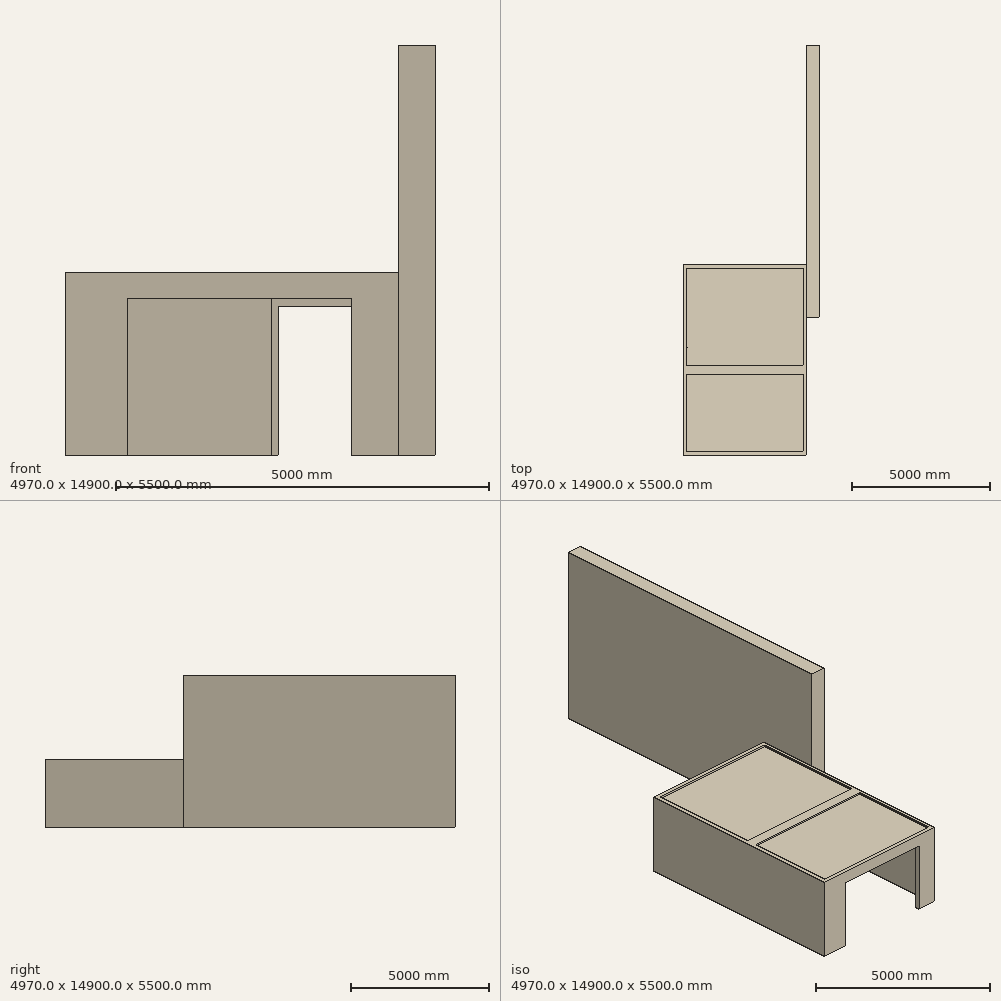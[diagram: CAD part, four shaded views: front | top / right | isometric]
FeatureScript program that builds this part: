
annotation { "Feature Type Name" : "Feature", "Feature Type Description" : "" }
export const myFeature = defineFeature(function(context is Context, id is Id, definition is map)
    precondition{}
    {
        {
            var Q0;
            Q0=qCreatedBy(makeId("Top.planeOp"),FACE);
            var sketch = newSketch(context, id + "F0", { "sketchPlane" : qUnion([Q0])});
            skLineSegment(sketch, "E0.rect.bottom", {"start": v(2235, -3475) * mm, "end": v(-2235, -3475) * mm});
            skLineSegment(sketch, "E0.rect.top", {"start": v(2235, 3475) * mm, "end": v(-2235, 3475) * mm});
            skLineSegment(sketch, "E0.rect.left", {"start": v(2235, -3475) * mm, "end": v(2235, 3475) * mm});
            skLineSegment(sketch, "E0.rect.right", {"start": v(-2235, -3475) * mm, "end": v(-2235, 3475) * mm});
            skPoint(sketch, "E0.rect.middle", {"position": v(0, 0) * mm});
            skLineSegment(sketch, "E1", {"start": v(2135, 3335) * mm, "end": v(-2095, 3335) * mm});
            skLineSegment(sketch, "E2", {"start": v(-2095, 3335) * mm, "end": v(-2095, -215) * mm});
            skLineSegment(sketch, "E3", {"start": v(-2095, -535) * mm, "end": v(-2095, -3335) * mm});
            skLineSegment(sketch, "E4", {"start": v(-2095, -3335) * mm, "end": v(2135, -3335) * mm});
            skLineSegment(sketch, "E5", {"start": v(-2095, -215) * mm, "end": v(-2095, -535) * mm});
            skLineSegment(sketch, "E6", {"start": v(-2095, -215) * mm, "end": v(1703, -215) * mm});
            skLineSegment(sketch, "E7", {"start": v(1703, -535) * mm, "end": v(-2095, -535) * mm});
            skLineSegment(sketch, "E8", {"start": v(2135, 3335) * mm, "end": v(2135, -215) * mm});
            skLineSegment(sketch, "E9", {"start": v(2135, -215) * mm, "end": v(1703, -215) * mm});
            skLineSegment(sketch, "E10", {"start": v(2135, -3335) * mm, "end": v(2135, -535) * mm});
            skLineSegment(sketch, "E11", {"start": v(2135, -535) * mm, "end": v(1703, -535) * mm});
            skLineSegment(sketch, "E12", {"start": v(1703, -215) * mm, "end": v(1703, -535) * mm});
            skSolve(sketch);
        }
        {
            var Q0;
            Q0=makeQuery(id+"F0.imprint","IMPRINT",FACE,{"disambiguationData":[TD([[makeQuery(id+"F0.imprint","IMPRINT",EDGE,{"derivedFrom":sQuery(id+"F0.wireOp",EDGE,"E0.rect.bottom")}),-1.0]])]});
            extrude(context, id + "F1", {"entities" : qUnion([Q0]), "oppositeDirection" : true, "depth" : 2280 * mm});
        }
        {
            var Q0;
            Q0=makeQuery(id+"F0.imprint","IMPRINT",FACE,{"disambiguationData":[TD([[makeQuery(id+"F0.imprint","IMPRINT",EDGE,{"derivedFrom":sQuery(id+"F0.wireOp",EDGE,"E5")}),1.0]])]});
            extrude(context, id + "F2", {"entities" : qUnion([Q0]), "operationType" : NewBodyOperationType.ADD, "oppositeDirection" : true, "depth" : 172 * mm});
        }
        {
            var Q0;
            Q0=makeQuery(id+"F2.boolean.opBoolean","MERGE",FACE,{"derivedFrom":[makeQuery(id+"F1.opExtrude","SWEPT_FACE",FACE,{"disambiguationData":[OSD([sQuery(id+"F0.wireOp",EDGE,"E11")])]}),makeQuery(id+"F2.opExtrude","SWEPT_FACE",FACE,{"disambiguationData":[OSD([sQuery(id+"F0.wireOp",EDGE,"E7")])]})]});
            var sketch = newSketch(context, id + "F3", { "sketchPlane" : qUnion([Q0])});
            skCircle(sketch, "E13", {"center": v(1935, -310) * mm, "radius": 75 * mm});
            skSolve(sketch);
        }
        {
            var Q0;
            Q0=makeQuery(id+"F3.imprint","IMPRINT",FACE,{"disambiguationData":[TD([[makeQuery(id+"F3.imprint","IMPRINT",EDGE,{"derivedFrom":sQuery(id+"F3.wireOp",EDGE,"E13")}),1.0]])]});
            extrude(context, id + "F4", {"entities" : qUnion([Q0]), "operationType" : NewBodyOperationType.REMOVE, "endBound" : BoundingType.UP_TO_NEXT, "oppositeDirection" : true, "depth" : 25 * mm});
        }
        {
            var Q0;
            Q0=makeQuery(id+"F1.opExtrude","SWEPT_FACE",FACE,{"disambiguationData":[OSD([sQuery(id+"F0.wireOp",EDGE,"E1")])]});
            var sketch = newSketch(context, id + "F5", { "sketchPlane" : qUnion([Q0])});
            skCircle(sketch, "E14", {"center": v(-1795, -135) * mm, "radius": 60 * mm});
            skCircle(sketch, "E15", {"center": v(-1595, -135) * mm, "radius": 60 * mm});
            skSolve(sketch);
        }
        {
            var Q0;
            Q0=makeQuery(id+"F5.imprint","IMPRINT",FACE,{"disambiguationData":[TD([[makeQuery(id+"F5.imprint","IMPRINT",EDGE,{"derivedFrom":sQuery(id+"F5.wireOp",EDGE,"E14")}),1.0]])]});
            var Q1;
            Q1=makeQuery(id+"F5.imprint","IMPRINT",FACE,{"disambiguationData":[TD([[makeQuery(id+"F5.imprint","IMPRINT",EDGE,{"derivedFrom":sQuery(id+"F5.wireOp",EDGE,"E15")}),1.0]])]});
            extrude(context, id + "F6", {"entities" : qUnion([Q0, Q1]), "operationType" : NewBodyOperationType.REMOVE, "endBound" : BoundingType.UP_TO_NEXT, "oppositeDirection" : true, "depth" : 25 * mm});
        }
        {
            var Q0;
            Q0=makeQuery(id+"F1.opExtrude","SWEPT_FACE",FACE,{"disambiguationData":[OSD([sQuery(id+"F0.wireOp",EDGE,"E0.rect.bottom")])]});
            var sketch = newSketch(context, id + "F7", { "sketchPlane" : qUnion([Q0])});
            skLineSegment(sketch, "E16", {"start": v(45.5, -2280) * mm, "end": v(-1398.66, -2280) * mm});
            skLineSegment(sketch, "E17", {"start": v(-1398.66, -2280) * mm, "end": v(-1398.66, -180) * mm});
            skLineSegment(sketch, "E18", {"start": v(-1398.66, -180) * mm, "end": v(0, -180) * mm});
            skLineSegment(sketch, "E19", {"start": v(0, -180) * mm, "end": v(1601.34, -180) * mm});
            skLineSegment(sketch, "E20", {"start": v(1601.34, -180) * mm, "end": v(1601.34, -2280) * mm});
            skLineSegment(sketch, "E21", {"start": v(1601.34, -2280) * mm, "end": v(45.5, -2280) * mm});
            skLineSegment(sketch, "E22", {"start": v(-2235, 0) * mm, "end": v(-2235, 124) * mm});
            skLineSegment(sketch, "E23", {"start": v(-2235, 124) * mm, "end": v(2235, 124) * mm});
            skLineSegment(sketch, "E24", {"start": v(2235, 124) * mm, "end": v(2235, 0) * mm});
            skLineSegment(sketch, "E25", {"start": v(-2235, 124) * mm, "end": v(-2235, 174) * mm});
            skLineSegment(sketch, "E26", {"start": v(-2235, 174) * mm, "end": v(2235, 174) * mm});
            skLineSegment(sketch, "E27", {"start": v(2235, 174) * mm, "end": v(2235, 124) * mm});
            skLineSegment(sketch, "E28", {"start": v(-2235, 0) * mm, "end": v(2235, 0) * mm});
            skSolve(sketch);
        }
        {
            var Q0;
            Q0=makeQuery(id+"F7.imprint","IMPRINT",FACE,{"disambiguationData":[TD([[makeQuery(id+"F7.imprint","IMPRINT",EDGE,{"derivedFrom":sQuery(id+"F7.wireOp",EDGE,"E16")}),-1.0]])]});
            extrude(context, id + "F8", {"entities" : qUnion([Q0]), "operationType" : NewBodyOperationType.REMOVE, "endBound" : BoundingType.UP_TO_NEXT, "oppositeDirection" : true, "depth" : 25 * mm});
        }
        {
            var Q0;
            Q0=makeQuery(id+"F1.opExtrude","SWEPT_FACE",FACE,{"disambiguationData":[OSD([sQuery(id+"F0.wireOp",EDGE,"E0.rect.top")])]});
            var sketch = newSketch(context, id + "F9", { "sketchPlane" : qUnion([Q0])});
            skLineSegment(sketch, "E29", {"start": v(-1625, -2280) * mm, "end": v(-1625, -280) * mm});
            skLineSegment(sketch, "E30", {"start": v(-1625, -280) * mm, "end": v(-625, -280) * mm});
            skLineSegment(sketch, "E31", {"start": v(-625, -280) * mm, "end": v(-625, -2280) * mm});
            skSolve(sketch);
        }
        {
            var Q0;
            {var subQ2=sQuery(id+"F9.wireOp",EDGE,"E29");Q0=makeQuery(id+"F9.imprint","IMPRINT",FACE,{"disambiguationData":[TD([[makeQuery(id+"F9.imprint","IMPRINT",EDGE,{"derivedFrom":subQ2}),-1.0]])]});}
            extrude(context, id + "F10", {"entities" : qUnion([Q0]), "operationType" : NewBodyOperationType.REMOVE, "endBound" : BoundingType.UP_TO_NEXT, "oppositeDirection" : true, "depth" : 25 * mm});
        }
        {
            var Q0;
            Q0=makeQuery(id+"F0.imprint","IMPRINT",FACE,{"disambiguationData":[TD([[makeQuery(id+"F0.imprint","IMPRINT",EDGE,{"derivedFrom":sQuery(id+"F0.wireOp",EDGE,"E0.rect.bottom")}),-1.0]])]});
            var Q1;
            Q1=makeQuery(id+"F0.imprint","IMPRINT",FACE,{"disambiguationData":[TD([[makeQuery(id+"F0.imprint","IMPRINT",EDGE,{"derivedFrom":sQuery(id+"F0.wireOp",EDGE,"E5")}),1.0]])]});
            extrude(context, id + "F11", {"entities" : qUnion([Q0, Q1]), "operationType" : NewBodyOperationType.ADD, "depth" : (2100 + 354 - 2280) * mm});
        }
        {
            var Q0;
            Q0=makeQuery(id+"F7.imprint","IMPRINT",FACE,{"disambiguationData":[TD([[makeQuery(id+"F7.imprint","IMPRINT",EDGE,{"derivedFrom":sQuery(id+"F7.wireOp",EDGE,"E22")}),-1.0]])]});
            var Q1;
            {var subQ0=sQuery(id+"F0.wireOp",EDGE,"E0.rect.top");Q1=makeQuery(id+"F11.boolean.opBoolean","MERGE",FACE,{"derivedFrom":[makeQuery(id+"F1.opExtrude","SWEPT_FACE",FACE,{"disambiguationData":[OSD([subQ0])]}),makeQuery(id+"F11.opExtrude","SWEPT_FACE",FACE,{"disambiguationData":[OSD([subQ0])]})]});}
            extrude(context, id + "F12", {"entities" : qUnion([Q0]), "operationType" : NewBodyOperationType.ADD, "endBound" : BoundingType.UP_TO_BODY, "oppositeDirection" : true, "endBoundEntityBody" : qUnion([Q1]), "depth" : 5554.66 * mm});
        }
        {
            var Q0;
            {var subQ0=sQuery(id+"F0.wireOp",EDGE,"E0.rect.left");Q0=makeQuery(id+"F11.boolean.opBoolean","MERGE",FACE,{"derivedFrom":[makeQuery(id+"F1.opExtrude","SWEPT_FACE",FACE,{"disambiguationData":[OSD([subQ0])]}),makeQuery(id+"F11.opExtrude","SWEPT_FACE",FACE,{"disambiguationData":[OSD([subQ0])]})]});}
            var sketch = newSketch(context, id + "F13", { "sketchPlane" : qUnion([Q0])});
            skLineSegment(sketch, "E32", {"start": v(1525, -2280) * mm, "end": v(1525, 3220) * mm});
            skLineSegment(sketch, "E33", {"start": v(1525, 3220) * mm, "end": v(11425, 3220) * mm});
            skLineSegment(sketch, "E34", {"start": v(11425, 3220) * mm, "end": v(11425, -2280) * mm});
            skLineSegment(sketch, "E35", {"start": v(11425, -2280) * mm, "end": v(1525, -2280) * mm});
            skSolve(sketch);
        }
        {
            var Q0;
            {var subQ8=sQuery(id+"F13.wireOp",EDGE,"E33");Q0=makeQuery(id+"F13.imprint","IMPRINT",FACE,{"disambiguationData":[TD([[makeQuery(id+"F13.imprint","IMPRINT",EDGE,{"derivedFrom":subQ8}),-1.0]])]});}
            var Q1;
            {var subQ0=sQuery(id+"F0.wireOp",EDGE,"E0.rect.left");var subQ4=sQuery(id+"F0.wireOp",EDGE,"E0.rect.top");var subQ5=makeQuery(id+"F11.boolean.opBoolean","MERGE",EDGE,{"derivedFrom":[makeQuery(id+"F1.opExtrude","SWEPT_EDGE",EDGE,{"disambiguationData":[OSD([subQ4,subQ0])]}),makeQuery(id+"F11.opExtrude","SWEPT_EDGE",EDGE,{"disambiguationData":[OSD([subQ4,subQ0])]})]});Q1=makeQuery(id+"F13.imprint","IMPRINT",FACE,{"disambiguationData":[TD([[makeQuery(id+"F13.imprint","IMPRINT",EDGE,{"derivedFrom":subQ5}),1.0]])]});}
            extrude(context, id + "F14", {"entities" : qUnion([Q0, Q1]), "depth" : 500 * mm});
        }
        {
            var Q0;
            {var subQ0=sQuery(id+"F0.wireOp",EDGE,"E1");Q0=makeQuery(id+"F12.boolean.opBoolean","SPLIT",FACE,{"disambiguationData":[TD([makeQuery(id+"F6.boolean.opBoolean","COPY",FACE,{"derivedFrom":makeQuery(id+"F6.opExtrude","SWEPT_FACE",FACE,{"disambiguationData":[OSD([sQuery(id+"F5.wireOp",EDGE,"E14")])]})})])],"derivedFrom":makeQuery(id+"F11.boolean.opBoolean","MERGE",FACE,{"derivedFrom":[makeQuery(id+"F1.opExtrude","SWEPT_FACE",FACE,{"disambiguationData":[OSD([subQ0])]}),makeQuery(id+"F11.opExtrude","SWEPT_FACE",FACE,{"disambiguationData":[OSD([subQ0])]})]})});}
            var sketch = newSketch(context, id + "F15", { "sketchPlane" : qUnion([Q0])});
            skLineSegment(sketch, "E36", {"start": v(525, -2280) * mm, "end": v(525, -180) * mm});
            skLineSegment(sketch, "E37", {"start": v(525, -180) * mm, "end": v(1725, -180) * mm});
            skLineSegment(sketch, "E38", {"start": v(1725, -180) * mm, "end": v(1725, -2280) * mm});
            skLineSegment(sketch, "E39", {"start": v(525, -2280) * mm, "end": v(1725, -2280) * mm});
            skSolve(sketch);
        }
        {
            var Q0;
            {var subQ14=sQuery(id+"F15.wireOp",EDGE,"E36");Q0=makeQuery(id+"F15.imprint","IMPRINT",FACE,{"disambiguationData":[TD([[makeQuery(id+"F15.imprint","IMPRINT",EDGE,{"derivedFrom":subQ14}),-1.0]])]});}
            extrude(context, id + "F16", {"entities" : qUnion([Q0]), "operationType" : NewBodyOperationType.REMOVE, "oppositeDirection" : true, "depth" : 65 * mm});
        }
        {
            var Q0;
            {var subQ0=sQuery(id+"F0.wireOp",EDGE,"E2");var subQ1=sQuery(id+"F0.wireOp",EDGE,"E3");var subQ2=sQuery(id+"F0.wireOp",EDGE,"E7");var subQ3=sQuery(id+"F0.wireOp",EDGE,"E11");var subQ4=sQuery(id+"F0.wireOp",EDGE,"E4");Q0=makeQuery(id+"F12.boolean.opBoolean","SPLIT",FACE,{"disambiguationData":[TD([makeQuery(id+"F1.opExtrude","SWEPT_FACE",FACE,{"disambiguationData":[OSD([subQ4])]}),makeQuery(id+"F1.opExtrude","SWEPT_FACE",FACE,{"disambiguationData":[OSD([subQ3])]}),makeQuery(id+"F2.opExtrude","SWEPT_FACE",FACE,{"disambiguationData":[OSD([subQ2])]}),makeQuery(id+"F11.opExtrude","CAP_FACE",FACE,{"disambiguationData":[OSD([sQuery(id+"F0.wireOp",EDGE,"E0.rect.bottom"),sQuery(id+"F0.wireOp",EDGE,"E0.rect.top"),sQuery(id+"F0.wireOp",EDGE,"E0.rect.left"),sQuery(id+"F0.wireOp",EDGE,"E0.rect.right"),sQuery(id+"F0.wireOp",EDGE,"E1"),subQ0,subQ1,subQ4,sQuery(id+"F0.wireOp",EDGE,"E6"),subQ2,sQuery(id+"F0.wireOp",EDGE,"E8"),sQuery(id+"F0.wireOp",EDGE,"E9"),sQuery(id+"F0.wireOp",EDGE,"E10"),subQ3])],"isStart":false}),makeQuery(id+"F11.opExtrude","SWEPT_FACE",FACE,{"disambiguationData":[OSD([subQ4])]}),makeQuery(id+"F11.opExtrude","SWEPT_FACE",FACE,{"disambiguationData":[OSD([subQ2,subQ3])]}),makeQuery(id+"F12.opExtrude","SWEPT_FACE",FACE,{"disambiguationData":[OSD([sQuery(id+"F7.wireOp",EDGE,"E23")])]})])],"derivedFrom":makeQuery(id+"F11.boolean.opBoolean","MERGE",FACE,{"derivedFrom":[makeQuery(id+"F1.opExtrude","SWEPT_FACE",FACE,{"disambiguationData":[OSD([subQ0,subQ1,sQuery(id+"F0.wireOp",EDGE,"E5")])]}),makeQuery(id+"F11.opExtrude","SWEPT_FACE",FACE,{"disambiguationData":[OSD([subQ0])]}),makeQuery(id+"F11.opExtrude","SWEPT_FACE",FACE,{"disambiguationData":[OSD([subQ1])]})]})});}
            var sketch = newSketch(context, id + "F17", { "sketchPlane" : qUnion([Q0])});
            skLineSegment(sketch, "E40", {"start": v(-3335, 149) * mm, "end": v(-535, 149) * mm, "construction": true});
            skCircle(sketch, "E41", {"center": v(-2385, 149) * mm, "radius": 15 * mm});
            skSolve(sketch);
        }
        {
            var Q0;
            Q0=makeQuery(id+"F17.imprint","IMPRINT",FACE,{"disambiguationData":[TD([[makeQuery(id+"F17.imprint","IMPRINT",EDGE,{"derivedFrom":sQuery(id+"F17.wireOp",EDGE,"E41")}),1.0]])]});
            extrude(context, id + "F18", {"entities" : qUnion([Q0]), "operationType" : NewBodyOperationType.ADD, "depth" : 10 * mm});
        }
        {
            var Q0;
            {var subQ0=sQuery(id+"F0.wireOp",EDGE,"E2");var subQ1=sQuery(id+"F0.wireOp",EDGE,"E3");var subQ2=sQuery(id+"F0.wireOp",EDGE,"E6");var subQ3=sQuery(id+"F0.wireOp",EDGE,"E9");var subQ4=sQuery(id+"F0.wireOp",EDGE,"E1");Q0=makeQuery(id+"F12.boolean.opBoolean","SPLIT",FACE,{"disambiguationData":[TD([makeQuery(id+"F1.opExtrude","SWEPT_FACE",FACE,{"disambiguationData":[OSD([subQ4])]}),makeQuery(id+"F1.opExtrude","SWEPT_FACE",FACE,{"disambiguationData":[OSD([subQ3])]}),makeQuery(id+"F2.opExtrude","SWEPT_FACE",FACE,{"disambiguationData":[OSD([subQ2])]}),makeQuery(id+"F11.opExtrude","CAP_FACE",FACE,{"disambiguationData":[OSD([sQuery(id+"F0.wireOp",EDGE,"E0.rect.bottom"),sQuery(id+"F0.wireOp",EDGE,"E0.rect.top"),sQuery(id+"F0.wireOp",EDGE,"E0.rect.left"),sQuery(id+"F0.wireOp",EDGE,"E0.rect.right"),subQ4,subQ0,subQ1,sQuery(id+"F0.wireOp",EDGE,"E4"),subQ2,sQuery(id+"F0.wireOp",EDGE,"E7"),sQuery(id+"F0.wireOp",EDGE,"E8"),subQ3,sQuery(id+"F0.wireOp",EDGE,"E10"),sQuery(id+"F0.wireOp",EDGE,"E11")])],"isStart":false}),makeQuery(id+"F11.opExtrude","SWEPT_FACE",FACE,{"disambiguationData":[OSD([subQ4])]}),makeQuery(id+"F11.opExtrude","SWEPT_FACE",FACE,{"disambiguationData":[OSD([subQ2,subQ3])]}),makeQuery(id+"F12.opExtrude","SWEPT_FACE",FACE,{"disambiguationData":[OSD([sQuery(id+"F7.wireOp",EDGE,"E23")])]})])],"derivedFrom":makeQuery(id+"F11.boolean.opBoolean","MERGE",FACE,{"derivedFrom":[makeQuery(id+"F1.opExtrude","SWEPT_FACE",FACE,{"disambiguationData":[OSD([subQ0,subQ1,sQuery(id+"F0.wireOp",EDGE,"E5")])]}),makeQuery(id+"F11.opExtrude","SWEPT_FACE",FACE,{"disambiguationData":[OSD([subQ0])]}),makeQuery(id+"F11.opExtrude","SWEPT_FACE",FACE,{"disambiguationData":[OSD([subQ1])]})]})});}
            var sketch = newSketch(context, id + "F19", { "sketchPlane" : qUnion([Q0])});
            skLineSegment(sketch, "E42", {"start": v(-215, 149) * mm, "end": v(3335, 149) * mm, "construction": true});
            skCircle(sketch, "E43", {"center": v(435, 149) * mm, "radius": 15 * mm});
            skSolve(sketch);
        }
        {
            var Q0;
            Q0=makeQuery(id+"F19.imprint","IMPRINT",FACE,{"disambiguationData":[TD([[makeQuery(id+"F19.imprint","IMPRINT",EDGE,{"derivedFrom":sQuery(id+"F19.wireOp",EDGE,"E43")}),1.0]])]});
            extrude(context, id + "F20", {"entities" : qUnion([Q0]), "operationType" : NewBodyOperationType.ADD, "depth" : 10 * mm});
        }
        {
            var Q0;
            {var subQ0=sQuery(id+"F0.wireOp",EDGE,"E10");Q0=makeQuery(id+"F12.boolean.opBoolean","SPLIT",FACE,{"disambiguationData":[TD([makeQuery(id+"F12.opExtrude","SWEPT_FACE",FACE,{"disambiguationData":[OSD([sQuery(id+"F7.wireOp",EDGE,"E23")])]})])],"derivedFrom":makeQuery(id+"F11.boolean.opBoolean","MERGE",FACE,{"derivedFrom":[makeQuery(id+"F1.opExtrude","SWEPT_FACE",FACE,{"disambiguationData":[OSD([subQ0])]}),makeQuery(id+"F11.opExtrude","SWEPT_FACE",FACE,{"disambiguationData":[OSD([subQ0])]})]})});}
            var sketch = newSketch(context, id + "F21", { "sketchPlane" : qUnion([Q0])});
            skLineSegment(sketch, "E44", {"start": v(3335, 149) * mm, "end": v(535, 149) * mm, "construction": true});
            skCircle(sketch, "E45", {"center": v(2365, 149) * mm, "radius": 15 * mm});
            skSolve(sketch);
        }
        {
            var Q0;
            Q0=makeQuery(id+"F21.imprint","IMPRINT",FACE,{"disambiguationData":[TD([[makeQuery(id+"F21.imprint","IMPRINT",EDGE,{"derivedFrom":sQuery(id+"F21.wireOp",EDGE,"E45")}),1.0]])]});
            extrude(context, id + "F22", {"entities" : qUnion([Q0]), "operationType" : NewBodyOperationType.ADD, "depth" : 10 * mm});
        }
        {
            var Q0;
            {var subQ0=sQuery(id+"F0.wireOp",EDGE,"E8");Q0=makeQuery(id+"F12.boolean.opBoolean","SPLIT",FACE,{"disambiguationData":[TD([makeQuery(id+"F12.opExtrude","SWEPT_FACE",FACE,{"disambiguationData":[OSD([sQuery(id+"F7.wireOp",EDGE,"E23")])]})])],"derivedFrom":makeQuery(id+"F11.boolean.opBoolean","MERGE",FACE,{"derivedFrom":[makeQuery(id+"F1.opExtrude","SWEPT_FACE",FACE,{"disambiguationData":[OSD([subQ0])]}),makeQuery(id+"F11.opExtrude","SWEPT_FACE",FACE,{"disambiguationData":[OSD([subQ0])]})]})});}
            var sketch = newSketch(context, id + "F23", { "sketchPlane" : qUnion([Q0])});
            skLineSegment(sketch, "E46", {"start": v(215, 149) * mm, "end": v(-3335, 149) * mm, "construction": true});
            skCircle(sketch, "E47", {"center": v(-470, 149) * mm, "radius": 15 * mm});
            skSolve(sketch);
        }
        {
            var Q0;
            Q0=makeQuery(id+"F23.imprint","IMPRINT",FACE,{"disambiguationData":[TD([[makeQuery(id+"F23.imprint","IMPRINT",EDGE,{"derivedFrom":sQuery(id+"F23.wireOp",EDGE,"E47")}),1.0]])]});
            extrude(context, id + "F24", {"entities" : qUnion([Q0]), "operationType" : NewBodyOperationType.ADD, "depth" : 10 * mm});
        }
    });
